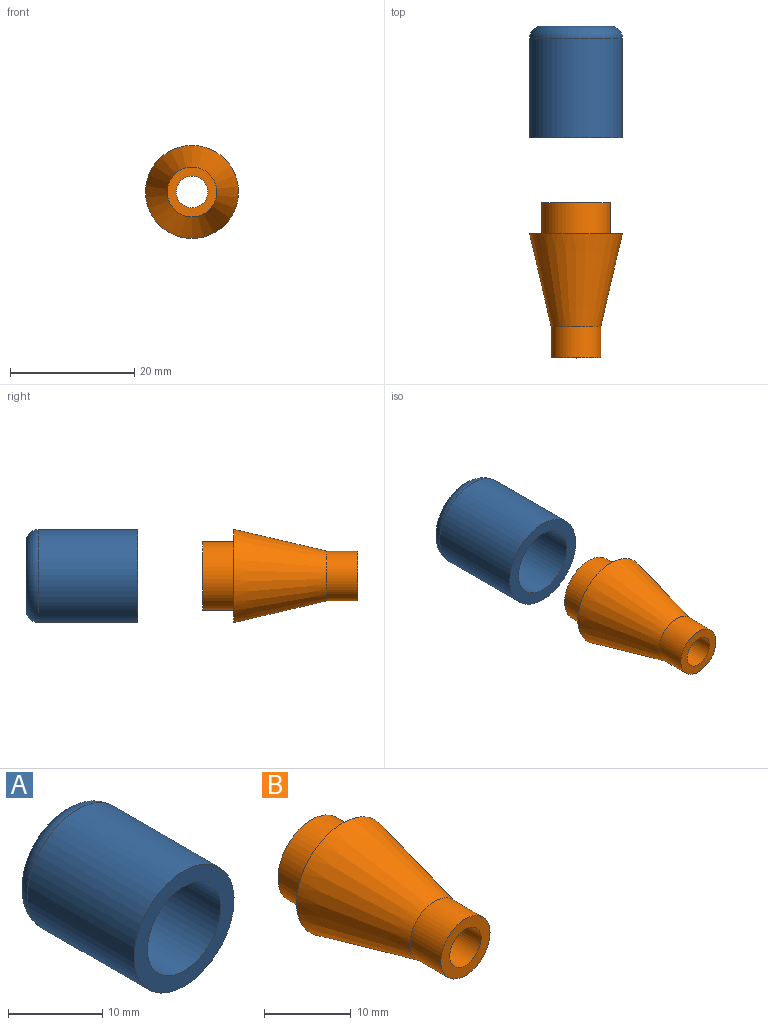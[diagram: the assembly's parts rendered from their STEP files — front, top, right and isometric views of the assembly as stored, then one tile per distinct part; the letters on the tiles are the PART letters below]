
ASSEMBLY  parts=2 mates=1
PART A: 8 faces, bbox 16.2x18x16.2 mm
  f0: cylinder r=3mm len=6mm, axis (0,1,0), area 0.9mm2, adj f3,f7
  f1: cylinder r=7.5mm len=16mm, axis (0,1,0), area 754mm2, adj f2,f4
  f2: plane 15x15mm, normal (0,-1,0), area 81.7mm2, adj f1,f5
  f3: plane 11x11mm, normal (0,1,0), area 66.8mm2, adj f0,f4
  f4: torus R=5.5mm, axis (0,-1,0), area 133.7mm2, adj f1,f3
  f5: cylinder r=5.5mm len=15.95mm, axis (0,-1,0), area 551.2mm2, adj f2,f6
  f6: plane 11x11mm, normal (0,-1,0), area 16.5mm2, adj f5,f7
  f7: cone r=3mm half-angle=45deg, axis (0,-1,0), area 71.1mm2, adj f0,f6
PART B: 9 faces, bbox 15x25x15 mm
  f0: plane 15x15mm, normal (0,1,0), area 81.7mm2, adj f1,f6
  f1: cone r=7.5mm half-angle=13.1deg, axis (0,1,0), area 556.5mm2, adj f0,f3
  f2: cylinder r=2.55mm len=15mm, axis (0,-1,0), area 240.3mm2, adj f4,f8
  f3: cylinder r=4mm len=8mm, axis (0,1,0), area 125.7mm2, adj f1,f4
  f4: plane 8x8mm, normal (0,-1,0), area 29.8mm2, adj f2,f3
  f5: plane 11x11mm, normal (0,1,0), area 50.9mm2, adj f6,f7
  f6: cylinder r=5.5mm len=11mm, axis (0,-1,0), area 172.8mm2, adj f0,f5
  f7: cylinder r=3.75mm len=10mm, axis (0,1,0), area 235.6mm2, adj f5,f8
  f8: plane 7.5x7.5mm, normal (0,1,0), area 23.8mm2, adj f2,f7
PLACE A t=(11.13,26.92,-3.17)mm
PLACE B t=(11.13,-6.57,-3.17)mm
MATE slider A.f1 <-> B.f1  axis (0,-1,0) through (11.13,8.92,-3.17)mm
